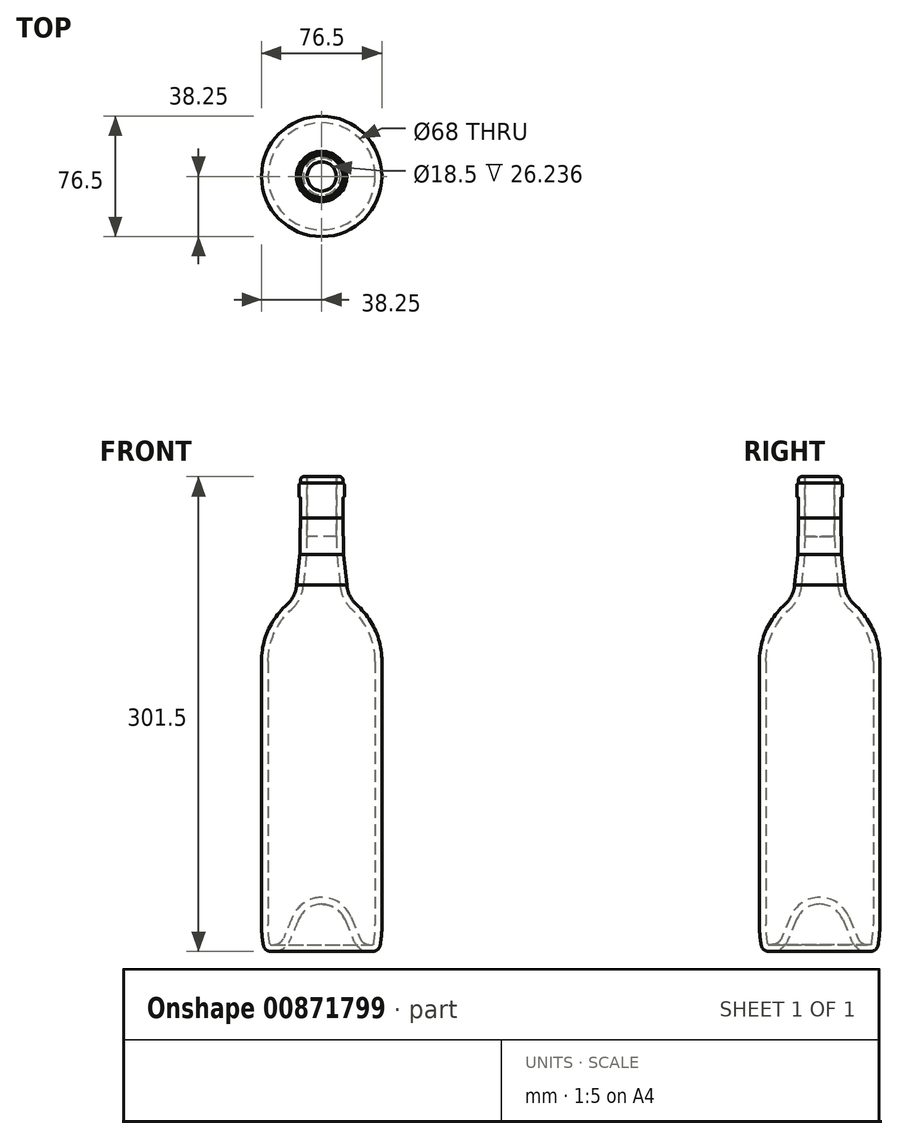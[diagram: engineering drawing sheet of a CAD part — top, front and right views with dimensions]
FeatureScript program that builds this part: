
annotation { "Feature Type Name" : "Feature", "Feature Type Description" : "" }
export const myFeature = defineFeature(function(context is Context, id is Id, definition is map)
    precondition{}
    {
        {
            var Q0;
            Q0=qCreatedBy(makeId("Front.planeOp"),FACE);
            var sketch = newSketch(context, id + "F0", { "sketchPlane" : qUnion([Q0])});
            skLineSegment(sketch, "E0", {"start": v(0, 0) * mm, "end": v(-38.25, 0) * mm, "construction": true});
            skLineSegment(sketch, "E1", {"start": v(-38.25, -81.03) * mm, "end": v(-38.25, 0) * mm, "construction": true});
            skLineSegment(sketch, "E2", {"start": v(0, 0) * mm, "end": v(0, 301.5) * mm, "construction": true});
            skLineSegment(sketch, "E3", {"start": v(-14.67, 20.24) * mm, "end": v(-20.31, 6.75) * mm});
            skLineSegment(sketch, "E4", {"start": v(-38.25, 17.1) * mm, "end": v(-38.25, 184.2) * mm});
            skArc(sketch, "E5.filletArc", {"start": v(-38.25, 17.1) * mm, "mid": v(-37.96, 10.49) * mm, "end": v(-37.1, 3.93) * mm});
            skArc(sketch, "E6.filletArc", {"start": v(-37.1, 3.93) * mm, "mid": v(-35.48, 1.11) * mm, "end": v(-32.42, 0) * mm});
            skArc(sketch, "E7.filletArc", {"start": v(-30.46, 0) * mm, "mid": v(-24.37, 1.84) * mm, "end": v(-20.31, 6.75) * mm});
            skArc(sketch, "E8.filletArc", {"start": v(0, 30) * mm, "mid": v(-8.8, 27.34) * mm, "end": v(-14.67, 20.24) * mm});
            skLineSegment(sketch, "E9", {"start": v(-11.47, 30) * mm, "end": v(10.28, 30) * mm, "construction": true});
            skLineSegment(sketch, "E10", {"start": v(-32.42, 0) * mm, "end": v(-30.46, 0) * mm});
            skArc(sketch, "E11", {"start": v(-38.25, 184.2) * mm, "mid": v(-34, 204.05) * mm, "end": v(-21.96, 220.41) * mm});
            skArc(sketch, "E12", {"start": v(-21.96, 220.41) * mm, "mid": v(-17.74, 225.96) * mm, "end": v(-15.95, 232.7) * mm});
            skLineSegment(sketch, "E13", {"start": v(-15.95, 232.7) * mm, "end": v(-13.9, 252) * mm});
            skLineSegment(sketch, "E14", {"start": v(-13.9, 252) * mm, "end": v(-13.5, 275.3) * mm});
            skLineSegment(sketch, "E15", {"start": v(-13.5, 275.3) * mm, "end": v(-13.5, 286) * mm});
            skArc(sketch, "E16", {"start": v(-13.5, 288) * mm, "mid": v(-13.63, 288.33) * mm, "end": v(-13.94, 288.5) * mm});
            skArc(sketch, "E17", {"start": v(-14.38, 289) * mm, "mid": v(-14.25, 288.66) * mm, "end": v(-13.94, 288.5) * mm});
            skArc(sketch, "E18", {"start": v(-14.23, 296.72) * mm, "mid": v(-14.34, 296.56) * mm, "end": v(-14.38, 296.37) * mm});
            skLineSegment(sketch, "E19", {"start": v(-14.38, 289) * mm, "end": v(-14.38, 296.37) * mm});
            skLineSegment(sketch, "E20", {"start": v(-13.5, 286) * mm, "end": v(-13.5, 288) * mm});
            skLineSegment(sketch, "E21", {"start": v(-14.23, 296.72) * mm, "end": v(-13.45, 297.5) * mm});
            skLineSegment(sketch, "E22", {"start": v(-13.45, 297.5) * mm, "end": v(-13.45, 299.5) * mm});
            skArc(sketch, "E23.filletArc", {"start": v(-11.45, 301.5) * mm, "mid": v(-12.86, 300.91) * mm, "end": v(-13.45, 299.5) * mm});
            skLineSegment(sketch, "E24", {"start": v(-11.45, 301.5) * mm, "end": v(-9.25, 301.5) * mm});
            skLineSegment(sketch, "E25", {"start": v(-9.25, 301.5) * mm, "end": v(-9.25, 275.26) * mm});
            skLineSegment(sketch, "E26.0", {"start": v(-9.65, 251.74) * mm, "end": v(-9.25, 275.26) * mm});
            skLineSegment(sketch, "E26.1", {"start": v(-11.72, 232.33) * mm, "end": v(-9.65, 251.74) * mm});
            skArc(sketch, "E26.2", {"start": v(-19.14, 217.23) * mm, "mid": v(-13.94, 224.05) * mm, "end": v(-11.72, 232.33) * mm});
            skArc(sketch, "E26.3", {"start": v(-34, 184.2) * mm, "mid": v(-30.11, 202.3) * mm, "end": v(-19.14, 217.23) * mm});
            skLineSegment(sketch, "E26.4", {"start": v(-34, 17.1) * mm, "end": v(-34, 184.2) * mm});
            skArc(sketch, "E26.5", {"start": v(-34, 17.1) * mm, "mid": v(-33.73, 10.86) * mm, "end": v(-32.92, 4.66) * mm});
            skArc(sketch, "E26.6", {"start": v(0, 34.25) * mm, "mid": v(-11.16, 30.88) * mm, "end": v(-18.59, 21.88) * mm});
            skLineSegment(sketch, "E26.7", {"start": v(-18.59, 21.88) * mm, "end": v(-24.23, 8.4) * mm});
            skArc(sketch, "E26.8", {"start": v(-30.46, 4.25) * mm, "mid": v(-26.72, 5.38) * mm, "end": v(-24.23, 8.4) * mm});
            skLineSegment(sketch, "E26.9", {"start": v(-32.42, 4.25) * mm, "end": v(-30.46, 4.25) * mm});
            skPoint(sketch, "E27.visualSharp", {"position": v(-32.84, 4.25) * mm});
            skArc(sketch, "E27.filletArc", {"start": v(-32.92, 4.66) * mm, "mid": v(-32.75, 4.37) * mm, "end": v(-32.42, 4.25) * mm});
            skLineSegment(sketch, "E28", {"start": v(0, 34.25) * mm, "end": v(0, 30) * mm});
            skSolve(sketch);
        }
        {
            var Q0;
            Q0 = qSketchRegion(id + "F0", true);
            var Q1;
            Q1=sQuery(id+"F0.wireOp",EDGE,"E2");
            revolve(context, id + "F1", {"surfaceOperationType" : NewSurfaceOperationType.NEW, "entities" : qUnion([Q0]), "axis" : qUnion([Q1]), "revolveType" : RevolveType.FULL});
        }
        {
            var Q0;
            Q0=makeQuery(id+"F1.opRevolve","SWEPT_FACE",FACE,{"disambiguationData":[OSD([sQuery(id+"F0.wireOp",EDGE,"E24")])]});
            var sketch = newSketch(context, id + "F2", { "sketchPlane" : qUnion([Q0])});
            skCircle(sketch, "E29.1", {"center": v(0, 0) * mm, "radius": 9.25 * mm});
            skSolve(sketch);
        }
        {
            var Q0;
            Q0=makeQuery(id+"F2.imprint","IMPRINT",FACE,{"disambiguationData":[TD([[makeQuery(id+"F2.imprint","IMPRINT",EDGE,{"derivedFrom":sQuery(id+"F2.wireOp",EDGE,"E29.1")}),-1.0]])]});
            extrude(context, id + "F3", {"entities" : qUnion([Q0]), "oppositeDirection" : true, "depth" : 38 * mm, "offsetDistance" : 25 * mm});
        }
        {
            var Q0;
            Q0=makeQuery(id+"F3.opExtrude","CAP_EDGE",EDGE,{"disambiguationData":[OSD([sQuery(id+"F2.wireOp",EDGE,"E29.1")])],"isStart":true});
            var Q1;
            Q1=makeQuery(id+"F3.opExtrude","CAP_EDGE",EDGE,{"disambiguationData":[OSD([sQuery(id+"F2.wireOp",EDGE,"E29.1")])],"isStart":false});
            fillet(context, id + "F4", {"entities" : qUnion([Q0, Q1]), "tangentPropagation" : true, "radius" : 0.5 * mm, "defaultsChanged" : false, "vertexSettings" : [], "allowEdgeOverflow" : false});
        }
    });
